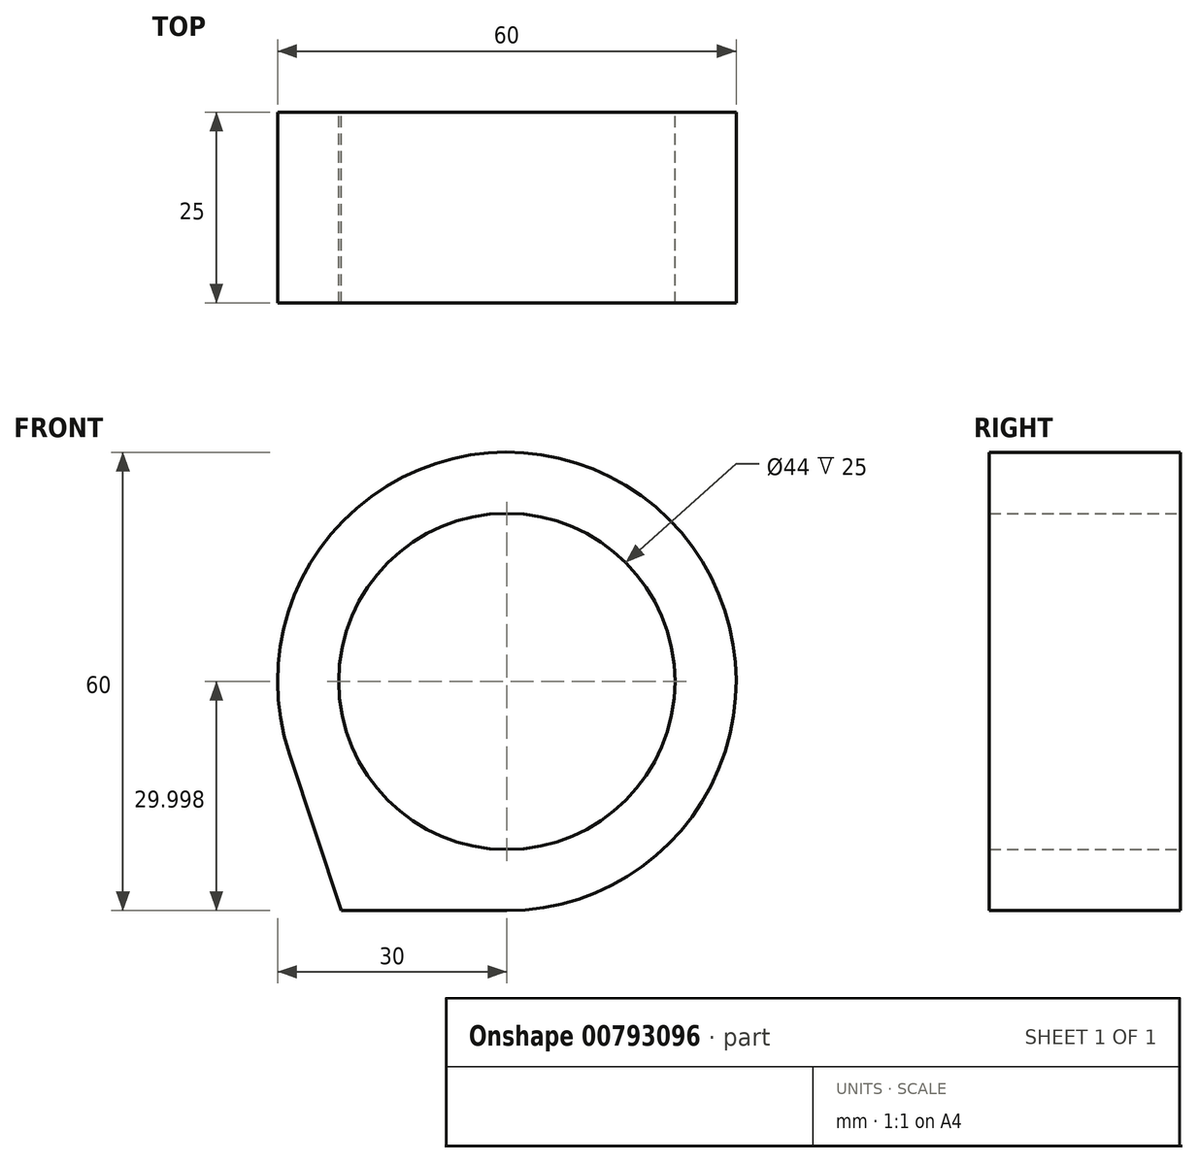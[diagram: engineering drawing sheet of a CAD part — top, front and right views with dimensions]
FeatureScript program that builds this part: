
annotation { "Feature Type Name" : "Feature", "Feature Type Description" : "" }
export const myFeature = defineFeature(function(context is Context, id is Id, definition is map)
    precondition{}
    {
        {
            var Q0;
            Q0=qCreatedBy(makeId("Front.planeOp"),FACE);
            var sketch = newSketch(context, id + "F0", { "sketchPlane" : qUnion([Q0])});
            skCircle(sketch, "E0", {"center": v(0, 11.24) * mm, "radius": 30 * mm});
            skCircle(sketch, "E1", {"center": v(0, 11.24) * mm, "radius": 22 * mm});
            skLineSegment(sketch, "E2", {"start": v(-28.47, 1.79) * mm, "end": v(-21.65, -18.76) * mm});
            skLineSegment(sketch, "E3", {"start": v(-21.65, -18.76) * mm, "end": v(79.12, -18.76) * mm});
            skLineSegment(sketch, "E4", {"start": v(0, 11.24) * mm, "end": v(69.6, 29.89) * mm, "construction": true});
            skLineSegment(sketch, "E5", {"start": v(0, 11.24) * mm, "end": v(69.6, 11.24) * mm, "construction": true});
            skLineSegment(sketch, "E6.trimOffspring", {"start": v(19.3, 21.8) * mm, "end": v(34.75, -6.4) * mm});
            skSolve(sketch);
        }
        {
            var Q0;
            Q0 = qSketchRegion(id + "F0", true);
            extrude(context, id + "F1", {"entities" : qUnion([Q0]), "depth" : 25 * mm, "offsetDistance" : 25 * mm});
        }
    });
